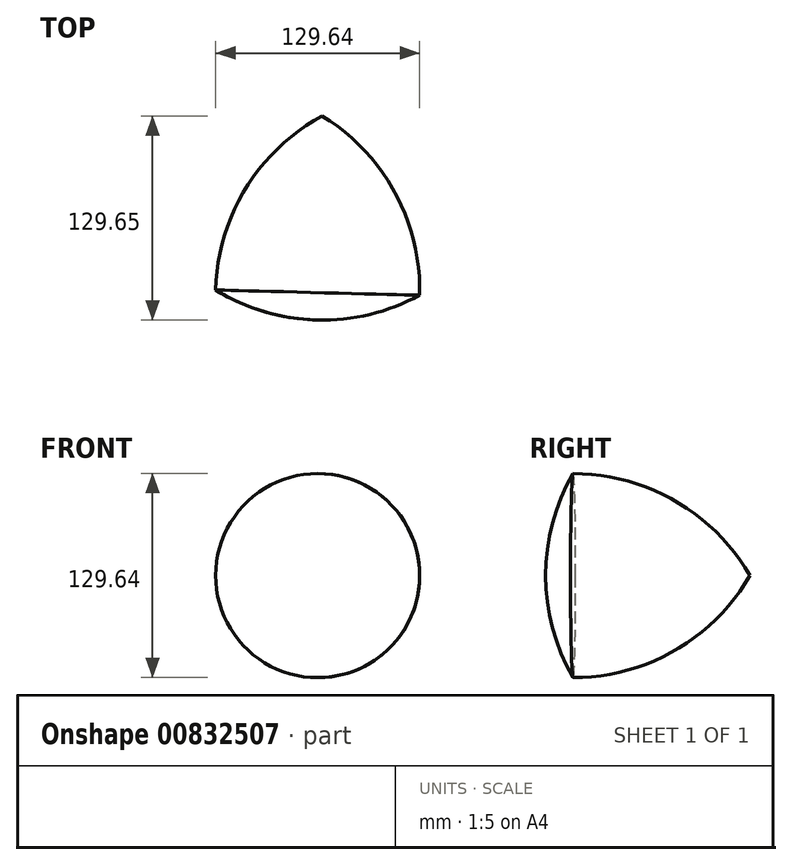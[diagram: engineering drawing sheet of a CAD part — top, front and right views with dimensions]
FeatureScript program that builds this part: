
annotation { "Feature Type Name" : "Feature", "Feature Type Description" : "" }
export const myFeature = defineFeature(function(context is Context, id is Id, definition is map)
    precondition{}
    {
        {
            var Q0;
            Q0=qCreatedBy(makeId("Top.planeOp"),FACE);
            var sketch = newSketch(context, id + "F0", { "sketchPlane" : qUnion([Q0])});
            skPoint(sketch, "E0.0.midPoint", {"position": v(-31.93, 19.53) * mm});
            skCircle(sketch, "E1", {"center": v(-65.75, -35.77) * mm, "radius": 129.65 * mm});
            skCircle(sketch, "E2", {"center": v(1.9, 74.83) * mm, "radius": 129.65 * mm});
            skCircle(sketch, "E3", {"center": v(63.85, -39.06) * mm, "radius": 129.65 * mm});
            skLineSegment(sketch, "E4", {"start": v(1.9, 74.83) * mm, "end": v(-1.4, -54.78) * mm});
            skSolve(sketch);
        }
        {
            var Q0;
            {var subQ0=sQuery(id+"F0.wireOp",EDGE,"E4");Q0=makeQuery(id+"F0.imprint","IMPRINT",FACE,{"disambiguationData":[TD([[makeQuery(id+"F0.imprint","IMPRINT",EDGE,{"derivedFrom":subQ0}),-1.0]])]});}
            var Q1;
            Q1=sQuery(id+"F0.wireOp",EDGE,"E4");
            revolve(context, id + "F1", {"surfaceOperationType" : NewSurfaceOperationType.NEW, "entities" : qUnion([Q0]), "axis" : qUnion([Q1]), "revolveType" : RevolveType.FULL});
        }
    });
